# Revit family: CIRQUA-L 1Xxxx-Mx-FSW
name_source: partatom
category: Oprawy oświetleniowe
units: mm (PartAtom-declared; Revit-internal decimal feet)

## family parameters
Numer OmniClass = 23.80.70.11
Obiekt nadrzędny = Powierzchnia
Punkt obliczania pomieszczeń = Nie
Tnij formami wycięć po wczytaniu = Nie
Typ części = Normalny
Tytuł OmniClass = Luminaries for Internal Lighting
Współdzielony = Nie
Wymiar okrągłego złącza = Użyj średnicy
Źródło światła = Tak

## types (9) — shared parameters
Emituj kształt widoczny w renderingu = Nie
Emituj ze średnicy okręgu = 76 mm  [stored 0.249344 ft]
Filtr koloru = 16777215
Kod zespołu = D5020200
Lampa = LED
Odchylenie kierunku = 90.00°
Plik sieci fotometrycznej = CIRQUA-L 1x3200-840 M.IES
Producent = RIDI Leuchten GmbH
URL = www.ridi.de
Zmiana temperatury barwowej przyciemniania lampy = <Brak>
brand = RIDI
conformity mark = CE
electrical safety class = 1
height = 171 mm  [stored 0.561024 ft]
ingress protection (IP) code = IP20
length = 310 mm  [stored 1.01706 ft]
nominal frequency = 50-60Hz
nominal voltage = 230
voltage type (AC, DC, UC) = AC
weight = 1,3 kg
width = 100 mm  [stored 0.328084 ft]
zero-valued in all types: Domyślna rzędna

## per-type parameters (varying)
| type | Model | Obciążenie pozorne | rated input power |
| CIRQUA-L 1X3000-830 M-FSW | 0321963AQ | 26 VA | 26 |
| CIRQUA-L 1X3600-830 M-FSW | 0321967AQ | 34 VA | 34 |
| CIRQUA-L 1X3600-830 M-DA-FSW | 0331967AQ | 34 VA | 34 |
| CIRQUA-L 1X3200-840 M-FSW | 0321951AQ | 26 VA | 26 |
| CIRQUA-L 1X3800-840 M-FSW | 0321955AQ | 34 VA | 34 |
| CIRQUA-L 1X3800-840 M-DA-FSW | 0331955AQ | 34 VA | 34 |
| CIRQUA-L 1X2600-930 M-FSW | 0321975AQ | 26 VA | 26 |
| CIRQUA-L 1X3100-930 M-FSW | 0321979AQ | 34 VA | 34 |
| CIRQUA-L 1X3100-930 M-DA-FSW | 0331979AQ | 34 VA | 34 |

note: column(s) folded — value = type name in every type: product name

note: [stored X ft] marks values corroborated as IEEE doubles in the binary element streams (Revit-internal decimal feet)
